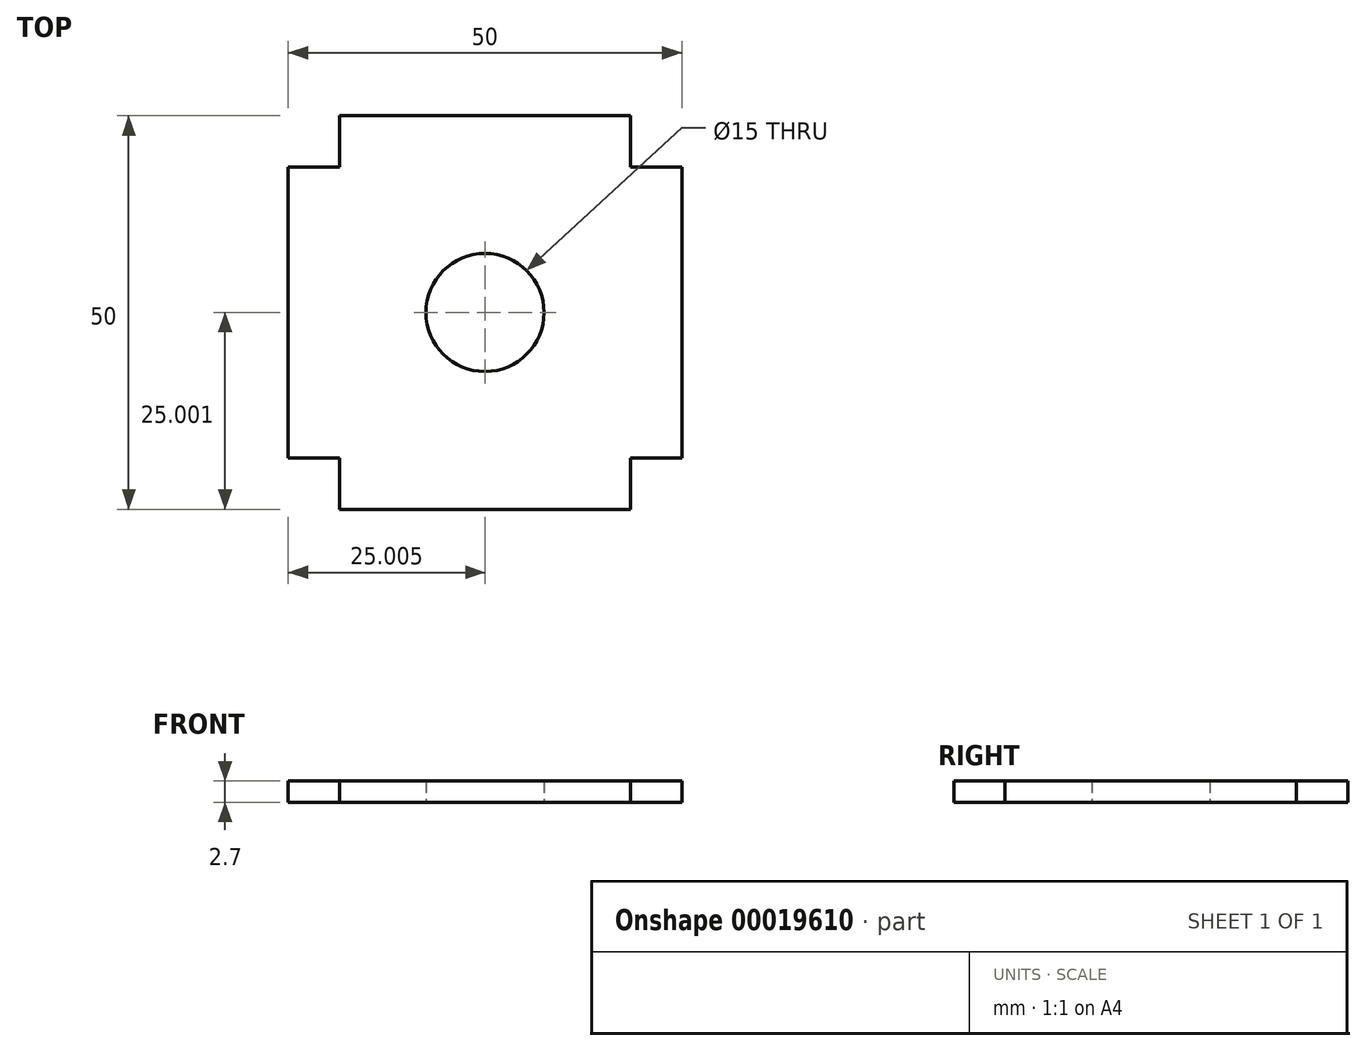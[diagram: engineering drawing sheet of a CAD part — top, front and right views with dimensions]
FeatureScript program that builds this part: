
annotation { "Feature Type Name" : "Feature", "Feature Type Description" : "" }
export const myFeature = defineFeature(function(context is Context, id is Id, definition is map)
    precondition{}
    {
        {
            var Q0;
            Q0=qCreatedBy(makeId("Top.planeOp"),FACE);
            var sketch = newSketch(context, id + "F0", { "sketchPlane" : qUnion([Q0])});
            skLineSegment(sketch, "E0", {"start": v(-27.68, 25.04) * mm, "end": v(9.32, 25.04) * mm});
            skLineSegment(sketch, "E1", {"start": v(9.32, 25.04) * mm, "end": v(9.32, 18.54) * mm});
            skLineSegment(sketch, "E2", {"start": v(9.32, 18.54) * mm, "end": v(15.82, 18.54) * mm});
            skLineSegment(sketch, "E3", {"start": v(15.82, 18.54) * mm, "end": v(15.82, -18.46) * mm});
            skLineSegment(sketch, "E4", {"start": v(15.82, -18.46) * mm, "end": v(9.32, -18.46) * mm});
            skLineSegment(sketch, "E5", {"start": v(9.32, -18.46) * mm, "end": v(9.32, -24.96) * mm});
            skLineSegment(sketch, "E6", {"start": v(9.32, -24.96) * mm, "end": v(-27.68, -24.96) * mm});
            skLineSegment(sketch, "E7", {"start": v(-27.68, -24.96) * mm, "end": v(-27.68, -18.46) * mm});
            skLineSegment(sketch, "E8", {"start": v(-27.68, -18.46) * mm, "end": v(-34.18, -18.46) * mm});
            skLineSegment(sketch, "E9", {"start": v(-34.18, -18.46) * mm, "end": v(-34.18, 18.54) * mm});
            skLineSegment(sketch, "E10", {"start": v(-34.18, 18.54) * mm, "end": v(-27.68, 18.54) * mm});
            skLineSegment(sketch, "E11", {"start": v(-27.68, 18.54) * mm, "end": v(-27.68, 25.04) * mm});
            skLineSegment(sketch, "E12", {"start": v(-9.18, 25.04) * mm, "end": v(-9.18, -24.96) * mm, "construction": true});
            skLineSegment(sketch, "E13", {"start": v(-34.18, 0.04) * mm, "end": v(15.82, 0.04) * mm, "construction": true});
            skCircle(sketch, "E14", {"center": v(-9.18, 0.04) * mm, "radius": 7.5 * mm});
            skSolve(sketch);
        }
        {
            var Q0;
            Q0=makeQuery(id+"F0.imprint","IMPRINT",FACE,{"disambiguationData":[TD([[makeQuery(id+"F0.imprint","IMPRINT",EDGE,{"derivedFrom":sQuery(id+"F0.wireOp",EDGE,"E0")}),-1.0]])]});
            extrude(context, id + "F1", {"entities" : qUnion([Q0]), "depth" : 2.7 * mm});
        }
    });
